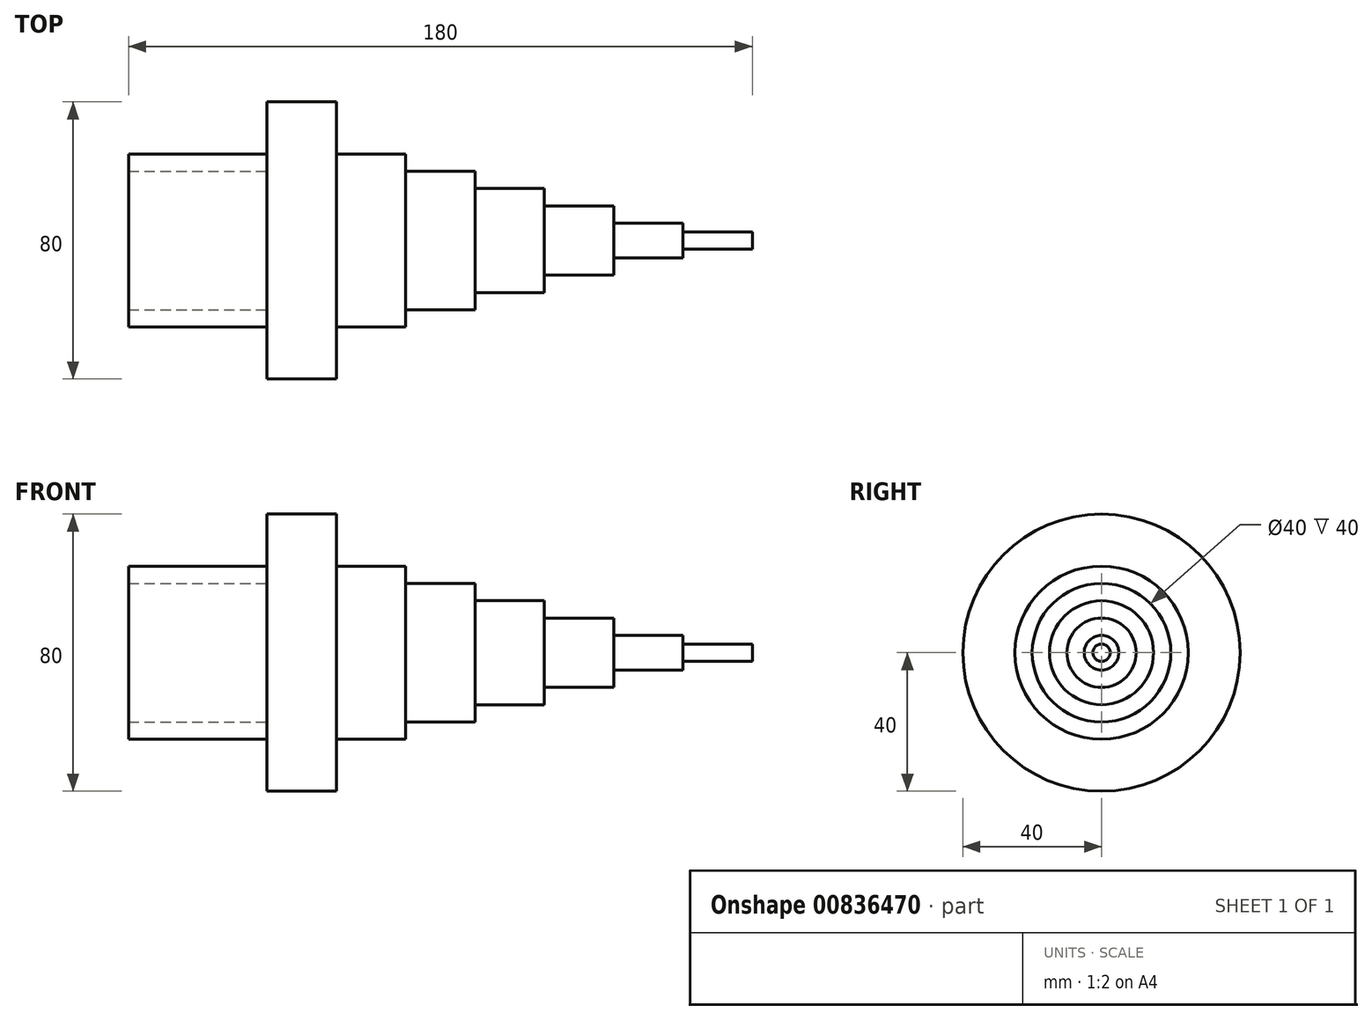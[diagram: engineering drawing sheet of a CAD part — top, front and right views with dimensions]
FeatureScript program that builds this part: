
annotation { "Feature Type Name" : "Feature", "Feature Type Description" : "" }
export const myFeature = defineFeature(function(context is Context, id is Id, definition is map)
    precondition{}
    {
        {
            var Q0;
            Q0=qCreatedBy(makeId("Front.planeOp"),FACE);
            var sketch = newSketch(context, id + "F0", { "sketchPlane" : qUnion([Q0])});
            skLineSegment(sketch, "E0.bottom", {"start": v(0, 0) * mm, "end": v(-40, 0) * mm});
            skLineSegment(sketch, "E0.top", {"start": v(0, 20) * mm, "end": v(-40, 20) * mm});
            skLineSegment(sketch, "E0.left", {"start": v(0, 0) * mm, "end": v(0, 20) * mm});
            skLineSegment(sketch, "E0.right", {"start": v(-40, 0) * mm, "end": v(-40, 20) * mm});
            skLineSegment(sketch, "E1.bottom", {"start": v(20, 0) * mm, "end": v(40, 0) * mm});
            skLineSegment(sketch, "E1.top", {"start": v(20, 25) * mm, "end": v(40, 25) * mm});
            skLineSegment(sketch, "E1.left", {"start": v(20, 0) * mm, "end": v(20, 25) * mm});
            skLineSegment(sketch, "E1.right", {"start": v(40, 0) * mm, "end": v(40, 25) * mm});
            skLineSegment(sketch, "E2.bottom", {"start": v(40, 0) * mm, "end": v(60, 0) * mm});
            skLineSegment(sketch, "E2.top", {"start": v(40, 20) * mm, "end": v(60, 20) * mm});
            skLineSegment(sketch, "E2.left", {"start": v(40, 0) * mm, "end": v(40, 20) * mm});
            skLineSegment(sketch, "E3.bottom", {"start": v(60, 0) * mm, "end": v(80, 0) * mm});
            skLineSegment(sketch, "E3.top", {"start": v(60, 15) * mm, "end": v(80, 15) * mm});
            skLineSegment(sketch, "E3.left", {"start": v(60, 0) * mm, "end": v(60, 15) * mm});
            skLineSegment(sketch, "E3.right", {"start": v(80, 0) * mm, "end": v(80, 15) * mm});
            skLineSegment(sketch, "E4", {"start": v(60, 20) * mm, "end": v(60, 15) * mm});
            skLineSegment(sketch, "E5.bottom", {"start": v(80, 0) * mm, "end": v(100, 0) * mm});
            skLineSegment(sketch, "E5.top", {"start": v(80, 10) * mm, "end": v(100, 10) * mm});
            skLineSegment(sketch, "E5.left", {"start": v(80, 0) * mm, "end": v(80, 10) * mm});
            skLineSegment(sketch, "E5.right", {"start": v(100, 0) * mm, "end": v(100, 10) * mm});
            skLineSegment(sketch, "E6.bottom", {"start": v(100, 0) * mm, "end": v(120, 0) * mm});
            skLineSegment(sketch, "E6.top", {"start": v(100, 5) * mm, "end": v(120, 5) * mm});
            skLineSegment(sketch, "E6.left", {"start": v(100, 0) * mm, "end": v(100, 5) * mm});
            skLineSegment(sketch, "E6.right", {"start": v(120, 0) * mm, "end": v(120, 5) * mm});
            skLineSegment(sketch, "E7.bottom", {"start": v(120, 0) * mm, "end": v(140, 0) * mm});
            skLineSegment(sketch, "E7.top", {"start": v(120, 2.5) * mm, "end": v(140, 2.5) * mm});
            skLineSegment(sketch, "E7.left", {"start": v(120, 0) * mm, "end": v(120, 2.5) * mm});
            skLineSegment(sketch, "E7.right", {"start": v(140, 0) * mm, "end": v(140, 2.5) * mm});
            skLineSegment(sketch, "E8.bottom", {"start": v(0, 0) * mm, "end": v(20, 0) * mm});
            skLineSegment(sketch, "E8.top", {"start": v(0, 40) * mm, "end": v(20, 40) * mm});
            skLineSegment(sketch, "E8.right", {"start": v(20, 0) * mm, "end": v(20, 40) * mm});
            skLineSegment(sketch, "E9.top", {"start": v(0, 25) * mm, "end": v(-40, 25) * mm});
            skLineSegment(sketch, "E9.right", {"start": v(-40, 0) * mm, "end": v(-40, 25) * mm});
            skLineSegment(sketch, "E10.trimOffspring", {"start": v(0, 25) * mm, "end": v(0, 40) * mm});
            skSolve(sketch);
        }
        {
            var Q0;
            {var subQ4=sQuery(id+"F0.wireOp",EDGE,"E0.top");Q0=makeQuery(id+"F0.imprint","IMPRINT",FACE,{"disambiguationData":[TD([[makeQuery(id+"F0.imprint","IMPRINT",EDGE,{"derivedFrom":subQ4}),-1.0]])]});}
            var Q1;
            {var subQ1=sQuery(id+"F0.wireOp",EDGE,"E1.bottom");Q1=makeQuery(id+"F0.imprint","IMPRINT",FACE,{"disambiguationData":[TD([[makeQuery(id+"F0.imprint","IMPRINT",EDGE,{"derivedFrom":subQ1}),1.0]])]});}
            var Q2;
            Q2=makeQuery(id+"F0.imprint","IMPRINT",FACE,{"disambiguationData":[TD([[makeQuery(id+"F0.imprint","IMPRINT",EDGE,{"derivedFrom":sQuery(id+"F0.wireOp",EDGE,"E2.bottom")}),1.0]])]});
            var Q3;
            Q3=makeQuery(id+"F0.imprint","IMPRINT",FACE,{"disambiguationData":[TD([[makeQuery(id+"F0.imprint","IMPRINT",EDGE,{"derivedFrom":sQuery(id+"F0.wireOp",EDGE,"E3.bottom")}),1.0]])]});
            var Q4;
            Q4=makeQuery(id+"F0.imprint","IMPRINT",FACE,{"disambiguationData":[TD([[makeQuery(id+"F0.imprint","IMPRINT",EDGE,{"derivedFrom":sQuery(id+"F0.wireOp",EDGE,"E5.bottom")}),1.0]])]});
            var Q5;
            Q5=makeQuery(id+"F0.imprint","IMPRINT",FACE,{"disambiguationData":[TD([[makeQuery(id+"F0.imprint","IMPRINT",EDGE,{"derivedFrom":sQuery(id+"F0.wireOp",EDGE,"E6.bottom")}),1.0]])]});
            var Q6;
            Q6=makeQuery(id+"F0.imprint","IMPRINT",FACE,{"disambiguationData":[TD([[makeQuery(id+"F0.imprint","IMPRINT",EDGE,{"derivedFrom":sQuery(id+"F0.wireOp",EDGE,"E7.bottom")}),1.0]])]});
            var Q7;
            Q7=sQuery(id+"F0.wireOp",EDGE,"E0.bottom");
            revolve(context, id + "F1", {"surfaceOperationType" : NewSurfaceOperationType.NEW, "entities" : qUnion([Q0, Q1, Q2, Q3, Q4, Q5, Q6]), "axis" : qUnion([Q7]), "revolveType" : RevolveType.FULL});
        }
    });
